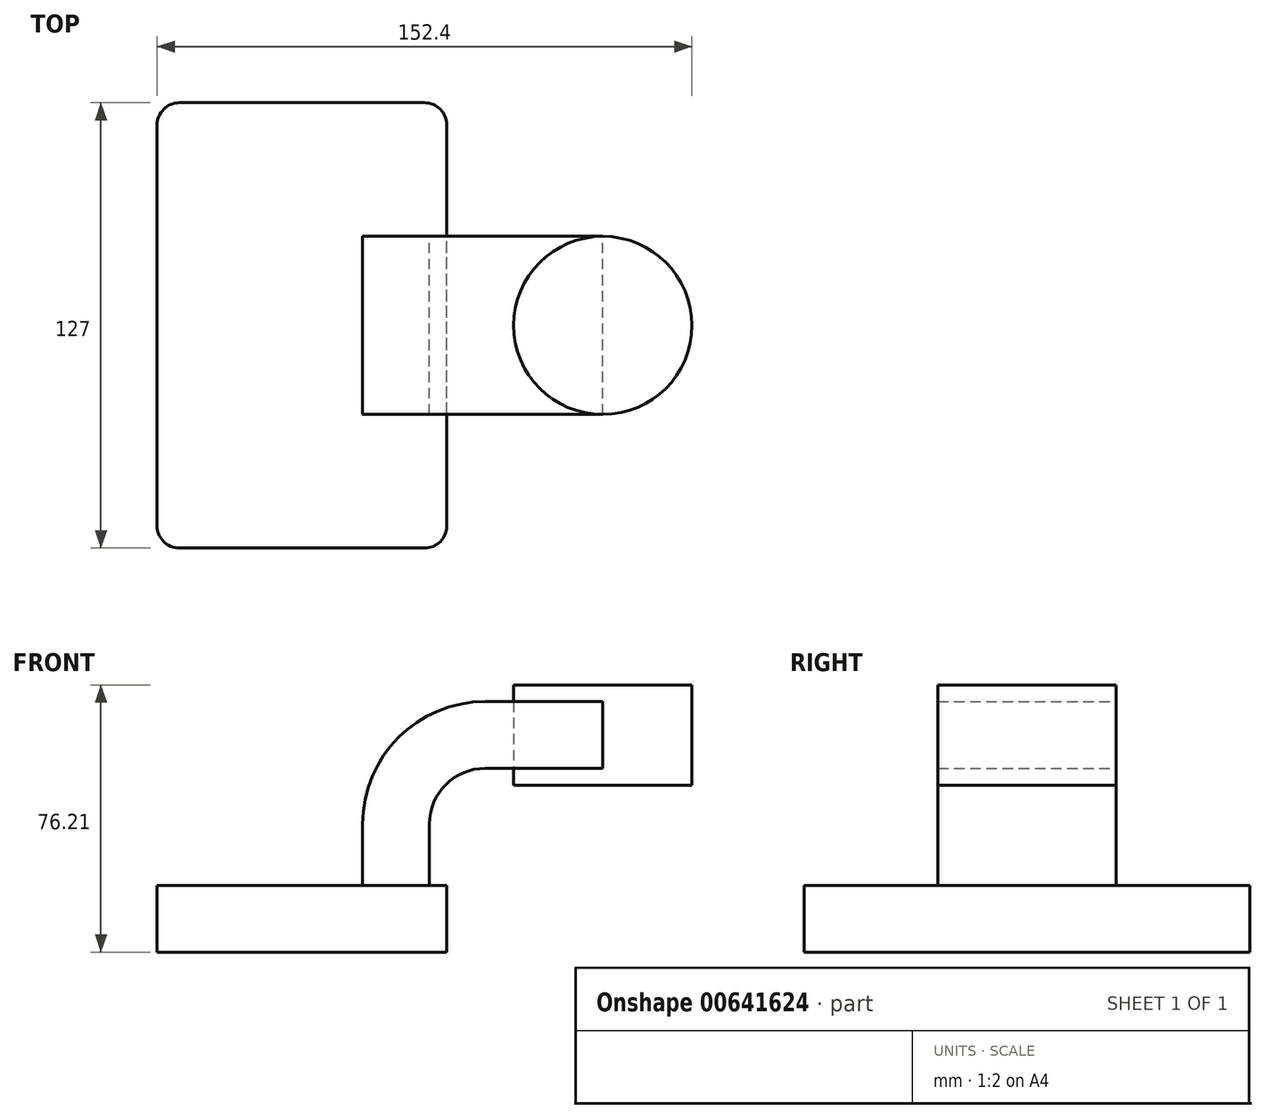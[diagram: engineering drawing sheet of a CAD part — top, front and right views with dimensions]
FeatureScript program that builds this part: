
annotation { "Feature Type Name" : "Feature", "Feature Type Description" : "" }
export const myFeature = defineFeature(function(context is Context, id is Id, definition is map)
    precondition{}
    {
        {
            var Q0;
            Q0=qCreatedBy(makeId("Front.planeOp"),FACE);
            var sketch = newSketch(context, id + "F0", { "sketchPlane" : qUnion([Q0])});
            skLineSegment(sketch, "E0.bottom", {"start": v(41.28, -9.52) * mm, "end": v(-41.28, -9.53) * mm});
            skLineSegment(sketch, "E0.top", {"start": v(41.28, 9.53) * mm, "end": v(-41.28, 9.52) * mm});
            skLineSegment(sketch, "E0.left", {"start": v(41.28, -9.52) * mm, "end": v(41.28, 9.53) * mm});
            skLineSegment(sketch, "E0.right", {"start": v(-41.28, -9.53) * mm, "end": v(-41.28, 9.52) * mm});
            skPoint(sketch, "E0.middle", {"position": v(0, 0) * mm});
            skLineSegment(sketch, "E1.bottom", {"start": v(111.12, 38.1) * mm, "end": v(60.32, 38.1) * mm});
            skLineSegment(sketch, "E1.top", {"start": v(111.12, 66.68) * mm, "end": v(60.32, 66.68) * mm});
            skLineSegment(sketch, "E1.left", {"start": v(111.12, 38.1) * mm, "end": v(111.12, 66.67) * mm});
            skLineSegment(sketch, "E1.right", {"start": v(60.32, 38.1) * mm, "end": v(60.32, 66.67) * mm});
            skPoint(sketch, "E1.middle", {"position": v(85.72, 52.39) * mm});
            skLineSegment(sketch, "E2", {"start": v(36.34, 9.53) * mm, "end": v(36.34, 27) * mm});
            skArc(sketch, "E3", {"start": v(36.34, 27) * mm, "mid": v(40.99, 38.23) * mm, "end": v(52.21, 42.88) * mm});
            skLineSegment(sketch, "E4", {"start": v(52.21, 42.88) * mm, "end": v(85.72, 42.88) * mm});
            skLineSegment(sketch, "E5.0", {"start": v(52.21, 61.93) * mm, "end": v(85.72, 61.93) * mm});
            skArc(sketch, "E5.1", {"start": v(17.29, 27) * mm, "mid": v(27.52, 51.7) * mm, "end": v(52.21, 61.93) * mm});
            skLineSegment(sketch, "E5.2", {"start": v(17.29, 9.53) * mm, "end": v(17.29, 27) * mm});
            skFitSpline(sketch, "E6", {"points": [v(-41.28, 9.52) * mm, v(52.21, 61.93) * mm], "startDerivative": vector(0.91, 97.5) * mm, "endDerivative": vector(119, -0.82) * mm});
            skLineSegment(sketch, "E7", {"start": v(85.72, 42.88) * mm, "end": v(85.72, 42.88) * mm});
            skLineSegment(sketch, "E8", {"start": v(85.72, 61.93) * mm, "end": v(85.72, 61.93) * mm});
            skLineSegment(sketch, "E9", {"start": v(85.72, 38.1) * mm, "end": v(85.72, 66.68) * mm});
            skSolve(sketch);
        }
        {
            var Q0;
            Q0=makeQuery(id+"F0.imprint","IMPRINT",FACE,{"disambiguationData":[TD([[makeQuery(id+"F0.imprint","IMPRINT",EDGE,{"derivedFrom":sQuery(id+"F0.wireOp",EDGE,"E0.bottom")}),-1.0]])]});
            extrude(context, id + "F1", {"entities" : qUnion([Q0]), "endBound" : BoundingType.SYMMETRIC, "depth" : 127 * mm, "offsetDistance" : 25.4 * mm});
        }
        {
            var Q0;
            {var subQ1=sQuery(id+"F0.wireOp",EDGE,"E2");Q0=makeQuery(id+"F0.imprint","IMPRINT",FACE,{"disambiguationData":[TD([[makeQuery(id+"F0.imprint","IMPRINT",EDGE,{"derivedFrom":subQ1}),1.0]])]});}
            var Q1;
            {var subQ0=sQuery(id+"F0.wireOp",EDGE,"E4");var subQ1=sQuery(id+"F0.wireOp",EDGE,"E1.right");var subQ2=makeQuery(id+"F0.imprint","INTERSECT",VERTEX,{"derivedFrom":[subQ1,subQ0]});Q1=makeQuery(id+"F0.imprint","IMPRINT",FACE,{"disambiguationData":[TD([[makeQuery(id+"F0.imprint","IMPRINT",EDGE,{"disambiguationData":[TD([[subQ2,-1.0]])],"derivedFrom":subQ1}),-1.0]])]});}
            extrude(context, id + "F2", {"entities" : qUnion([Q0, Q1]), "operationType" : NewBodyOperationType.ADD, "endBound" : BoundingType.SYMMETRIC, "depth" : 50.8 * mm, "offsetDistance" : 25.4 * mm});
        }
        {
            var Q0;
            Q0=makeQuery(id+"F0.imprint","IMPRINT",FACE,{"disambiguationData":[TD([[makeQuery(id+"F0.imprint","IMPRINT",EDGE,{"derivedFrom":sQuery(id+"F0.wireOp",EDGE,"E5.1")}),1.0]])]});
            extrude(context, id + "F3", {"entities" : qUnion([Q0]), "operationType" : NewBodyOperationType.ADD, "endBound" : BoundingType.SYMMETRIC, "depth" : 25.4 * mm, "offsetDistance" : 25.4 * mm});
        }
        {
            var Q0;
            {var subQ0=sQuery(id+"F0.wireOp",EDGE,"E1.left");Q0=makeQuery(id+"F0.imprint","IMPRINT",FACE,{"disambiguationData":[TD([[makeQuery(id+"F0.imprint","IMPRINT",EDGE,{"derivedFrom":subQ0}),1.0]])]});}
            var Q1;
            Q1=sQuery(id+"F0.wireOp",EDGE,"E9");
            revolve(context, id + "F4", {"entities" : qUnion([Q0]), "axis" : qUnion([Q1]), "revolveType" : RevolveType.FULL});
        }
        {
            var Q0;
            Q0=makeQuery(id+"F1.opExtrude","CAP_EDGE",EDGE,{"disambiguationData":[OSD([sQuery(id+"F0.wireOp",EDGE,"E0.left")])],"isStart":false});
            var Q1;
            Q1=makeQuery(id+"F1.opExtrude","CAP_EDGE",EDGE,{"disambiguationData":[OSD([sQuery(id+"F0.wireOp",EDGE,"E0.right")])],"isStart":false});
            var Q2;
            Q2=makeQuery(id+"F1.opExtrude","CAP_EDGE",EDGE,{"disambiguationData":[OSD([sQuery(id+"F0.wireOp",EDGE,"E0.left")])],"isStart":true});
            var Q3;
            Q3=makeQuery(id+"F1.opExtrude","CAP_EDGE",EDGE,{"disambiguationData":[OSD([sQuery(id+"F0.wireOp",EDGE,"E0.right")])],"isStart":true});
            fillet(context, id + "F5", {"entities" : qUnion([Q0, Q1, Q2, Q3]), "radius" : 6.35 * mm, "tangentPropagation" : true, "allowEdgeOverflow" : false});
        }
    });
